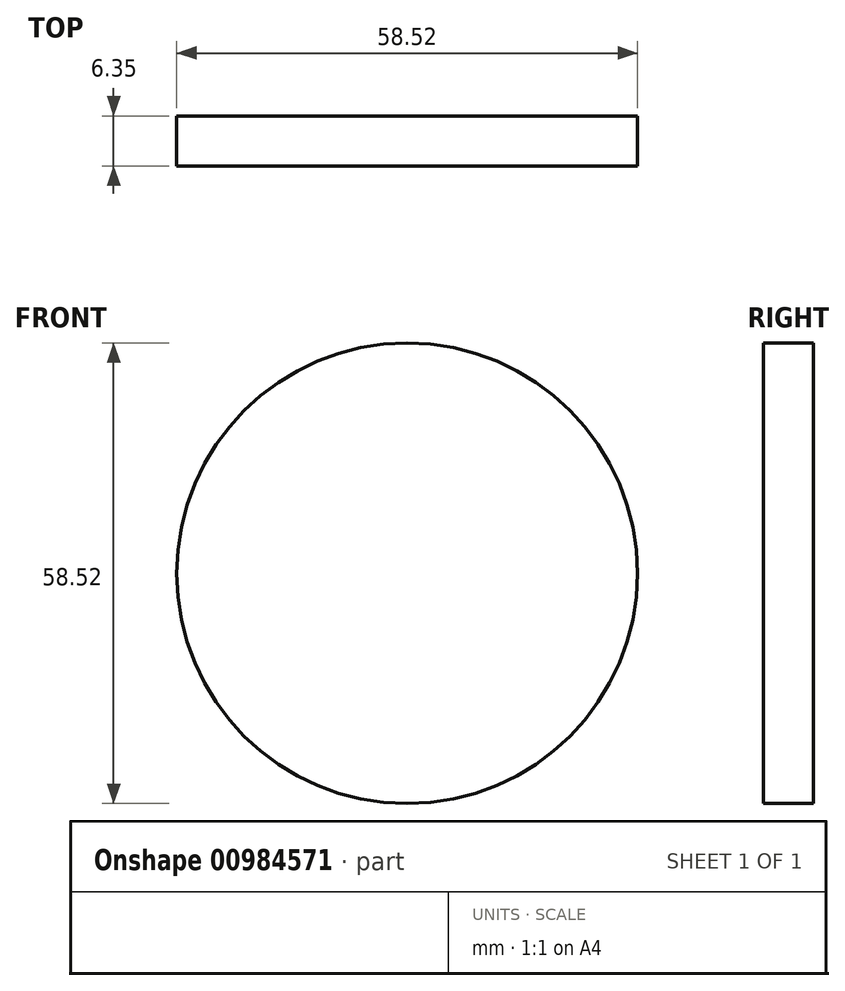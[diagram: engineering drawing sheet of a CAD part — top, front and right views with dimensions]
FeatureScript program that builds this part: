
annotation { "Feature Type Name" : "Feature", "Feature Type Description" : "" }
export const myFeature = defineFeature(function(context is Context, id is Id, definition is map)
    precondition{}
    {
        {
            var Q0;
            Q0=qCreatedBy(makeId("Front.planeOp"),FACE);
            var sketch = newSketch(context, id + "F0", { "sketchPlane" : qUnion([Q0])});
            skArc(sketch, "E0", {"start": v(-59.72, 66.21) * mm, "mid": v(-99.4, 68.47) * mm, "end": v(-103.39, 28.94) * mm});
            skCircle(sketch, "E1", {"center": v(-14.22, 14.94) * mm, "radius": 29.26 * mm});
            skArc(sketch, "E2", {"start": v(88.88, 65.39) * mm, "mid": v(49.2, 67.65) * mm, "end": v(45.21, 28.11) * mm});
            skArc(sketch, "E3", {"start": v(-103.83, -21.12) * mm, "mid": v(-65.97, -66.23) * mm, "end": v(-8.14, -77.3) * mm});
            skSolve(sketch);
        }
        {
            var Q0;
            Q0=makeQuery(id+"F0.imprint","IMPRINT",FACE,{"disambiguationData":[TD([[makeQuery(id+"F0.imprint","IMPRINT",EDGE,{"derivedFrom":sQuery(id+"F0.wireOp",EDGE,"E1")}),1.0]])]});
            extrude(context, id + "F1", {"entities" : qUnion([Q0]), "depth" : 6.35 * mm, "offsetDistance" : 25.4 * mm});
        }
    });
